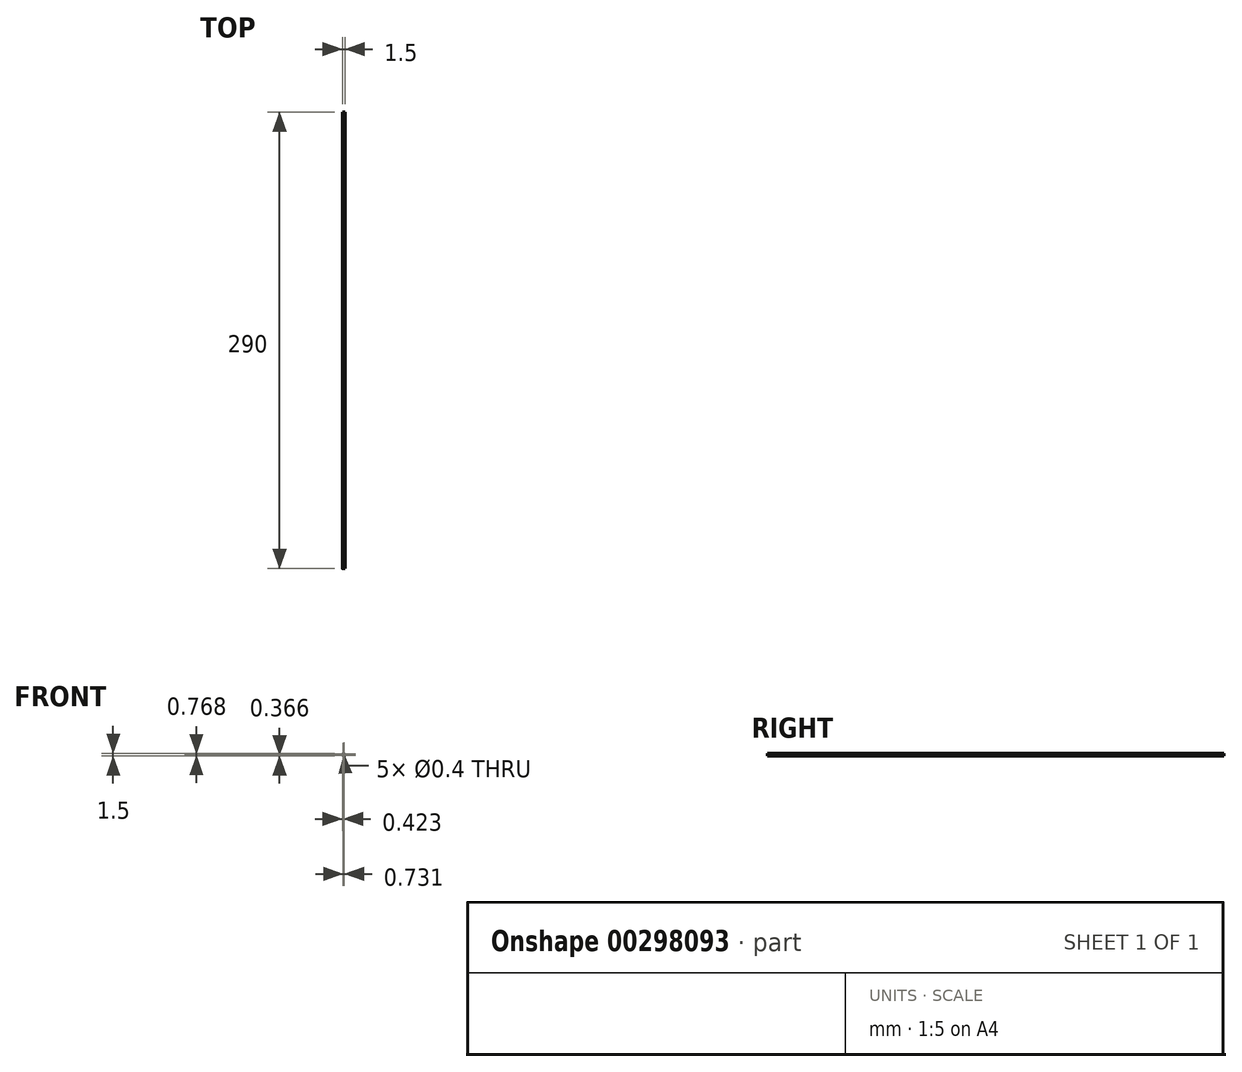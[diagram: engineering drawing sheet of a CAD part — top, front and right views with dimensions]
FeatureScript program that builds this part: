
annotation { "Feature Type Name" : "Feature", "Feature Type Description" : "" }
export const myFeature = defineFeature(function(context is Context, id is Id, definition is map)
    precondition{}
    {
        {
            var Q0;
            Q0=qCreatedBy(makeId("Front.planeOp"),FACE);
            var sketch = newSketch(context, id + "F0", { "sketchPlane" : qUnion([Q0])});
            skCircle(sketch, "E0", {"center": v(0.4, 0) * mm, "radius": 0.2 * mm});
            skCircle(sketch, "E1.1.0", {"center": v(0.12, 0.38) * mm, "radius": 0.2 * mm});
            skCircle(sketch, "E1.2.0", {"center": v(-0.33, 0.24) * mm, "radius": 0.2 * mm});
            skCircle(sketch, "E1.3.0", {"center": v(-0.33, -0.24) * mm, "radius": 0.2 * mm});
            skCircle(sketch, "E1.4.0", {"center": v(0.12, -0.38) * mm, "radius": 0.2 * mm});
            skPoint(sketch, "E1.center", {"position": v(0, 0) * mm});
            skCircle(sketch, "E2", {"center": v(0, 0) * mm, "radius": 0.75 * mm});
            skSolve(sketch);
        }
        {
            var Q0;
            Q0=makeQuery(id+"F0.imprint","IMPRINT",FACE,{"disambiguationData":[TD([[makeQuery(id+"F0.imprint","IMPRINT",EDGE,{"derivedFrom":sQuery(id+"F0.wireOp",EDGE,"E0")}),-1.0]])]});
            extrude(context, id + "F1", {"entities" : qUnion([Q0]), "depth" : 290 * mm});
        }
    });
